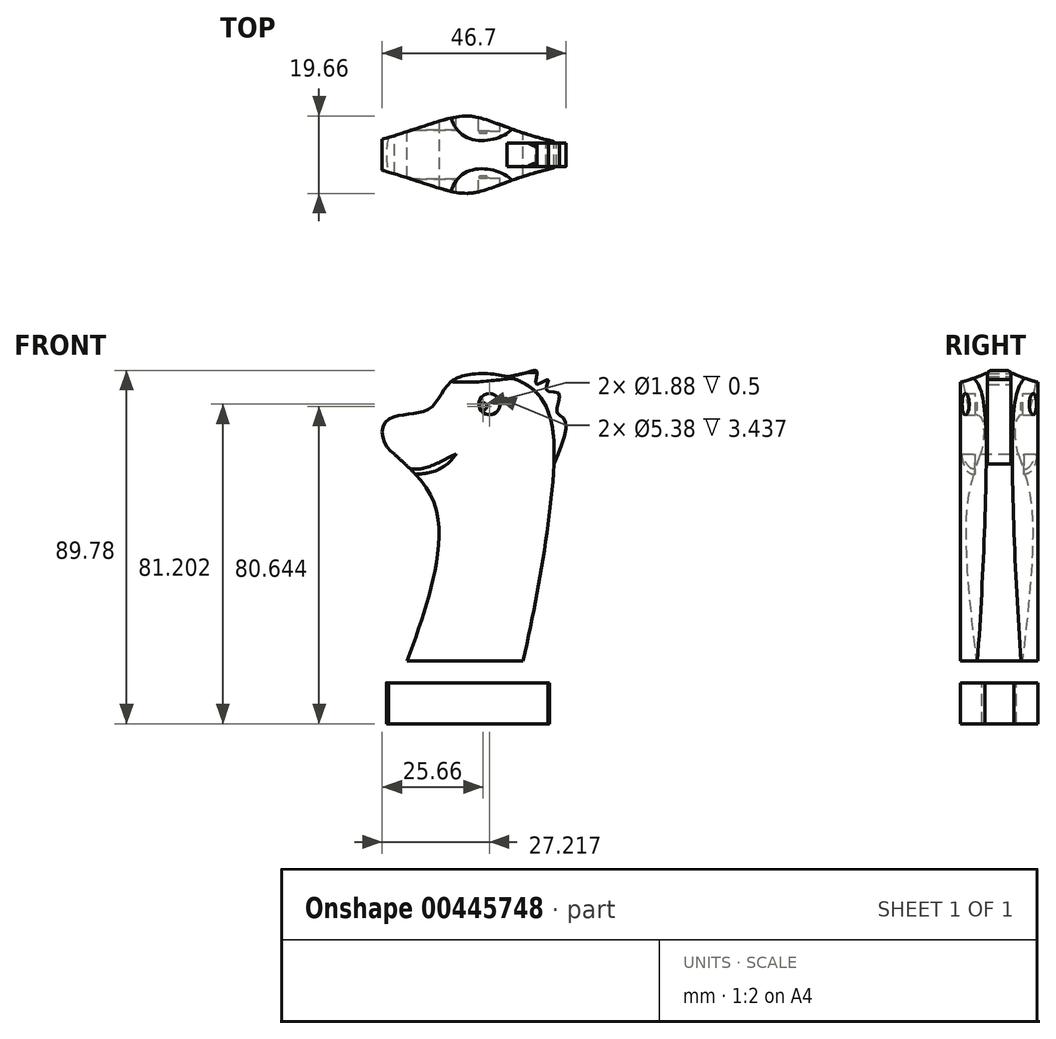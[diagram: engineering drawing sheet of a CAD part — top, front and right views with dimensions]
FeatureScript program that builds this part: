
annotation { "Feature Type Name" : "Feature", "Feature Type Description" : "" }
export const myFeature = defineFeature(function(context is Context, id is Id, definition is map)
    precondition{}
    {
        {
            var Q0;
            Q0=qCreatedBy(makeId("Front.planeOp"),FACE);
            var sketch = newSketch(context, id + "F0", { "sketchPlane" : qUnion([Q0])});
            skLineSegment(sketch, "E0", {"start": v(-15.47, -26.41) * mm, "end": v(14.04, -26.41) * mm});
            skLineSegment(sketch, "E1.left", {"start": v(0, -26.41) * mm, "end": v(0, -42.4) * mm});
            skLineSegment(sketch, "E2", {"start": v(-15.47, -26.41) * mm, "end": v(0, -26.41) * mm});
            skLineSegment(sketch, "E3.bottom", {"start": v(-20.68, -42.4) * mm, "end": v(20.68, -42.4) * mm});
            skLineSegment(sketch, "E3.top", {"start": v(-20.68, -31.96) * mm, "end": v(20.68, -31.96) * mm});
            skLineSegment(sketch, "E3.left", {"start": v(-20.68, -42.4) * mm, "end": v(-20.68, -31.96) * mm});
            skLineSegment(sketch, "E3.right", {"start": v(20.68, -42.4) * mm, "end": v(20.68, -31.96) * mm});
            skPoint(sketch, "E3.middle", {"position": v(0, -37.18) * mm});
            skLineSegment(sketch, "E4", {"start": v(-15.47, -26.41) * mm, "end": v(-20.68, -31.96) * mm});
            skFitSpline(sketch, "E5", {"points": [v(-15.47, -26.41) * mm, v(-9.64, -8.83) * mm, v(-8.2, 12.67) * mm, v(-18.66, 26.1) * mm], "startDerivative": vector(18.69, 50.32) * mm, "endDerivative": vector(-41.68, 37.54) * mm});
            skFitSpline(sketch, "E6", {"points": [v(-18.66, 26.1) * mm, v(-20.81, 34.45) * mm, v(-10.02, 37.48) * mm, v(-4.05, 44.7) * mm, v(12.21, 45.06) * mm, v(20.73, 36.03) * mm, v(20.8, 11.67) * mm, v(14.04, -26.41) * mm], "startDerivative": vector(-87.85, 57) * mm, "endDerivative": vector(-41.58, -182.29) * mm});
            skFitSpline(sketch, "E7", {"points": [v(9.9, 45.8) * mm, v(13.34, 46.47) * mm, v(15.44, 46.98) * mm, v(17.53, 47.1) * mm, v(17.38, 43.84) * mm, v(20.39, 45.06) * mm, v(19.98, 42.4) * mm, v(23.11, 41.6) * mm, v(22.56, 37.03) * mm, v(24.64, 34.8) * mm, v(21.88, 23.6) * mm], "startDerivative": vector(38.88, 3.13) * mm, "endDerivative": vector(-31.16, -77.09) * mm});
            skCircle(sketch, "E8", {"center": v(5.46, 38.8) * mm, "radius": 2.69 * mm});
            skFitSpline(sketch, "E9", {"points": [v(-13.33, 21) * mm, v(-2.98, 26.18) * mm], "startDerivative": vector(16.07, 0.72) * mm, "endDerivative": vector(6.72, 9.76) * mm});
            skFitSpline(sketch, "E10", {"points": [v(-2.98, 26.18) * mm, v(-14.7, 22.43) * mm], "startDerivative": vector(-11.7, -5.37) * mm, "endDerivative": vector(-11.96, 2.29) * mm});
            skCircle(sketch, "E11", {"center": v(3.9, 38.24) * mm, "radius": 0.94 * mm});
            skSolve(sketch);
        }
        {
            var Q0;
            Q0=makeQuery(id+"F0.imprint","IMPRINT",FACE,{"disambiguationData":[TD([[makeQuery(id+"F0.imprint","IMPRINT",EDGE,{"derivedFrom":sQuery(id+"F0.wireOp",EDGE,"E1.top")}),-1.0]])]});
            var Q1;
            {var subQ5=sQuery(id+"F0.wireOp",EDGE,"E3.left");Q1=makeQuery(id+"F0.imprint","IMPRINT",FACE,{"disambiguationData":[TD([[makeQuery(id+"F0.imprint","IMPRINT",EDGE,{"derivedFrom":subQ5}),-1.0]])]});}
            var Q2;
            {var subQ0=sQuery(id+"F0.wireOp",EDGE,"E2");Q2=makeQuery(id+"F0.imprint","IMPRINT",FACE,{"disambiguationData":[TD([[makeQuery(id+"F0.imprint","IMPRINT",EDGE,{"derivedFrom":subQ0}),-1.0]])]});}
            var Q3;
            Q3=sQuery(id+"F0.wireOp",EDGE,"E1.left");
            revolve(context, id + "F1", {"entities" : qUnion([Q0, Q1, Q2]), "axis" : qUnion([Q3]), "revolveType" : RevolveType.FULL});
        }
        {
            var Q0;
            {var subQ3=sQuery(id+"F0.wireOp",EDGE,"E0");Q0=makeQuery(id+"F0.imprint","IMPRINT",FACE,{"disambiguationData":[TD([[makeQuery(id+"F0.imprint","IMPRINT",EDGE,{"derivedFrom":subQ3}),1.0]])]});}
            extrude(context, id + "F2", {"entities" : qUnion([Q0]), "endBound" : BoundingType.SYMMETRIC, "depth" : 20 * mm});
        }
        {
            var Q0;
            Q0=qCreatedBy(makeId("Top.planeOp"),FACE);
            var sketch = newSketch(context, id + "F3", { "sketchPlane" : qUnion([Q0])});
            skLineSegment(sketch, "E12", {"start": v(41.36, 0) * mm, "end": v(26.76, 0) * mm});
            skLineSegment(sketch, "E13.bottom", {"start": v(-60.9, 35.7) * mm, "end": v(60.9, 35.7) * mm});
            skLineSegment(sketch, "E13.top", {"start": v(-60.9, -35.7) * mm, "end": v(60.9, -35.7) * mm});
            skLineSegment(sketch, "E13.left", {"start": v(-60.9, 35.7) * mm, "end": v(-60.9, -35.7) * mm});
            skLineSegment(sketch, "E13.right", {"start": v(60.9, 35.7) * mm, "end": v(60.9, -35.7) * mm});
            skPoint(sketch, "E13.middle", {"position": v(0, 0) * mm});
            skPoint(sketch, "E14.2.internal.snap0", {"position": v(34.06, 0) * mm});
            skFitSpline(sketch, "E14", {"points": [v(41.36, 0) * mm, v(0, 9.82) * mm, v(-38.92, 0) * mm], "startDerivative": vector(-169.88, 19.23) * mm, "endDerivative": vector(-146.2, -26.88) * mm});
            skFitSpline(sketch, "E15.MirrorCS", {"points": [v(41.36, 0) * mm, v(0, -9.82) * mm, v(-38.92, 0) * mm], "startDerivative": vector(-169.88, -19.23) * mm, "endDerivative": vector(-146.2, 26.88) * mm});
            skSolve(sketch);
        }
        {
            var Q0;
            Q0 = qSketchRegion(id + "F3", true);
            extrude(context, id + "F4", {"entities" : qUnion([Q0]), "operationType" : NewBodyOperationType.REMOVE, "endBound" : BoundingType.SYMMETRIC, "oppositeDirection" : true, "depth" : 200 * mm});
        }
        {
            var Q0;
            {var subQ0=sQuery(id+"F0.wireOp",EDGE,"E7");Q0=makeQuery(id+"F0.imprint","IMPRINT",FACE,{"disambiguationData":[TD([[makeQuery(id+"F0.imprint","IMPRINT",EDGE,{"derivedFrom":subQ0}),-1.0]])]});}
            extrude(context, id + "F5", {"entities" : qUnion([Q0]), "operationType" : NewBodyOperationType.ADD, "endBound" : BoundingType.SYMMETRIC, "depth" : 6 * mm});
        }
        {
            var Q0;
            {var subQ0=sQuery(id+"F0.wireOp",EDGE,"E9");Q0=makeQuery(id+"F0.imprint","IMPRINT",FACE,{"disambiguationData":[TD([[makeQuery(id+"F0.imprint","IMPRINT",EDGE,{"derivedFrom":subQ0}),1.0]])]});}
            extrude(context, id + "F6", {"entities" : qUnion([Q0]), "operationType" : NewBodyOperationType.ADD, "endBound" : BoundingType.SYMMETRIC, "depth" : 12.5 * mm});
        }
        {
            var Q0;
            Q0=qCreatedBy(makeId("Right.planeOp"),FACE);
            var sketch = newSketch(context, id + "F7", { "sketchPlane" : qUnion([Q0])});
            skFitSpline(sketch, "E16", {"points": [v(0, 49.15) * mm, v(19.25, 16.8) * mm], "startDerivative": vector(28.9, -30.17) * mm, "endDerivative": vector(-69.72, -93.94) * mm});
            skLineSegment(sketch, "E17", {"start": v(0, 49.15) * mm, "end": v(0, 61.14) * mm});
            skFitSpline(sketch, "E18.MirrorCS", {"points": [v(0, 49.15) * mm, v(-19.25, 16.8) * mm], "startDerivative": vector(-28.9, -30.17) * mm, "endDerivative": vector(69.72, -93.94) * mm});
            skLineSegment(sketch, "E19.bottom", {"start": v(28.64, 66.13) * mm, "end": v(-29.56, 66.13) * mm});
            skLineSegment(sketch, "E19.top", {"start": v(28.64, -56.18) * mm, "end": v(-29.56, -56.18) * mm});
            skLineSegment(sketch, "E19.left", {"start": v(28.64, 66.13) * mm, "end": v(28.64, -56.18) * mm});
            skLineSegment(sketch, "E19.right", {"start": v(-29.56, 66.13) * mm, "end": v(-29.56, -56.18) * mm});
            skLineSegment(sketch, "E20", {"start": v(19.25, 16.8) * mm, "end": v(28.64, 14.36) * mm});
            skLineSegment(sketch, "E21", {"start": v(-19.25, 16.8) * mm, "end": v(-29.56, 16.8) * mm});
            skPoint(sketch, "E21.endSnap0", {"position": v(-29.56, 4.97) * mm});
            skSolve(sketch);
        }
        {
            var Q0;
            Q0=makeQuery(id+"F7.imprint","IMPRINT",FACE,{"disambiguationData":[TD([[makeQuery(id+"F7.imprint","IMPRINT",EDGE,{"derivedFrom":sQuery(id+"F7.wireOp",EDGE,"E16")}),1.0]])]});
            extrude(context, id + "F8", {"entities" : qUnion([Q0]), "operationType" : NewBodyOperationType.REMOVE, "endBound" : BoundingType.THROUGH_ALL, "depth" : 80 * mm, "hasSecondDirection" : true, "secondDirectionBound" : SecondDirectionBoundingType.THROUGH_ALL, "secondDirectionOppositeDirection" : true, "secondDirectionDepth" : 25 * mm});
        }
        {
            var Q0;
            Q0=makeQuery(id+"F0.imprint","IMPRINT",FACE,{"disambiguationData":[TD([[makeQuery(id+"F0.imprint","IMPRINT",EDGE,{"derivedFrom":sQuery(id+"F0.wireOp",EDGE,"E8")}),1.0]])]});
            extrude(context, id + "F9", {"entities" : qUnion([Q0]), "operationType" : NewBodyOperationType.ADD, "endBound" : BoundingType.SYMMETRIC, "depth" : 12 * mm});
        }
        {
            var Q0;
            Q0=makeQuery(id+"F0.imprint","IMPRINT",FACE,{"disambiguationData":[TD([[makeQuery(id+"F0.imprint","IMPRINT",EDGE,{"derivedFrom":sQuery(id+"F0.wireOp",EDGE,"E11")}),1.0]])]});
            extrude(context, id + "F10", {"entities" : qUnion([Q0]), "operationType" : NewBodyOperationType.ADD, "endBound" : BoundingType.SYMMETRIC, "depth" : 11 * mm});
        }
    });
